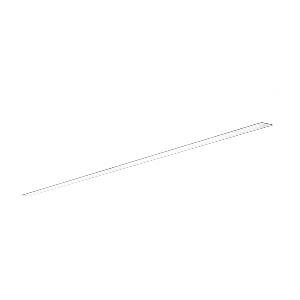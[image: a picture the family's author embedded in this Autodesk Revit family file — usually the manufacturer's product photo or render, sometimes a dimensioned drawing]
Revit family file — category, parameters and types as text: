
# Revit family: dotoo_line_-_dle_3000_830_d_00808229_bd82
name_source: partatom
category: Lighting Fixtures
units: mm (PartAtom-declared; Revit-internal decimal feet)

## family parameters
Cut with Voids When Loaded = No
Host = Face
Light Source = No
Part Type = Normal
Room Calculation Point = No
Round Connector Dimension = Use Diameter
Shared = No

## types (1)
- DOTOO.line - DLE 3000/830/D (1 x LED, 2650 lm, 3000K)
    Apparent Load = 26 VA
    Approval mark = CE
    CIE Flux Codes = 67 91 98 100 100
    Color Rendering = 80-89
    Color Temperature = 3000K
    Control Gear = Electronic ballast
    Default Elevation = 1800 mm
    Description = DLE 3000/830/D|Recessed luminaire|light source:  |work equipment: Adjustable electronic ballast, digital DALI|connected load: 220-240 V, 50/60 Hz|Power consumption: approx. 26 W|standby: approx. 0,20|power factor: approx. 0,970|luminous flux: 2650 lm|luminous efficacy: 101 lm/W|light distribution: Direct|direct ratio: approx. 100 %|colour temperature: Warm white, ca. 3000 K|color rendering index (CRI): >= 80|chromaticity tolerance:  3 SDCM|System of protection: IP 40|class of protection: I|technology: Continuously dimmable|operation: External|luminaire body|material: Sectional aluminium|colour: White|lamp cover: Acrylic (PMMA), Clear|weight (net): approx. 7.3 kg|mains lead: Connector|Fastening: Fastening bow|glare control: Prism aperture|luminance(L65): <= 3000 cd/m|unified glare rating(4H 8H): <=  19|special features: DALI Load 1x, TouchDIM - dimming via standard switch, Flicker-free, Suitable as emergency lighting|
    Frequency = 50 Hz
    Height = 0 mm  [stored 0 ft]
    Lamp = 1 x LED
    Lamp Light Flux = 2650 lm
    Lamp count = 1
    Length = 2256 mm
    Luminous efficacy = 102 lm/W
    Manufacturer = Waldmann
    ModVariant = No
    Model = 00808229
    Mounting Place = Ceiling
    Mounting Type = Recessed
    Number of Poles = 1
    OnlyDefault = Yes
    Power Factor = 1
    Product Name = DOTOO.line - DLE 3000/830/D
    Product group = Recessed luminaire
    ProductGroupID = 4
    Protection Class = Protection class I
    Protection Degree = IP 40
    RLX_Detail_Level = 1
    RLX_Emergency_Light_Flux = 0 lm
    RLX_Emergency_Type = 0
    RLX_Emergency_Type_DB = No
    RlxData = <blob elided: 14605 chars, md5=e1a0e1f3>
    Socket = socket
    Standby Power = 0 W
    System Light Flux = 2650 lm
    System Power = 26 W
    Type Comments = Product without accessories
    Type Image = 114407000-00808225.jpg
    URL = http://relux.com
    VarID = ---
    Voltage = 230 V
    Voltage Range = 220-240 V
    Weight = 0.00 kg
    Width = 60 mm  [stored 0.19685 ft]

note: [stored X ft] marks values corroborated as IEEE doubles in the binary element streams (Revit-internal decimal feet)

## geometry (parser evidence)
native form markers: Sweep x10
no freeform markers — native parametric forms only
